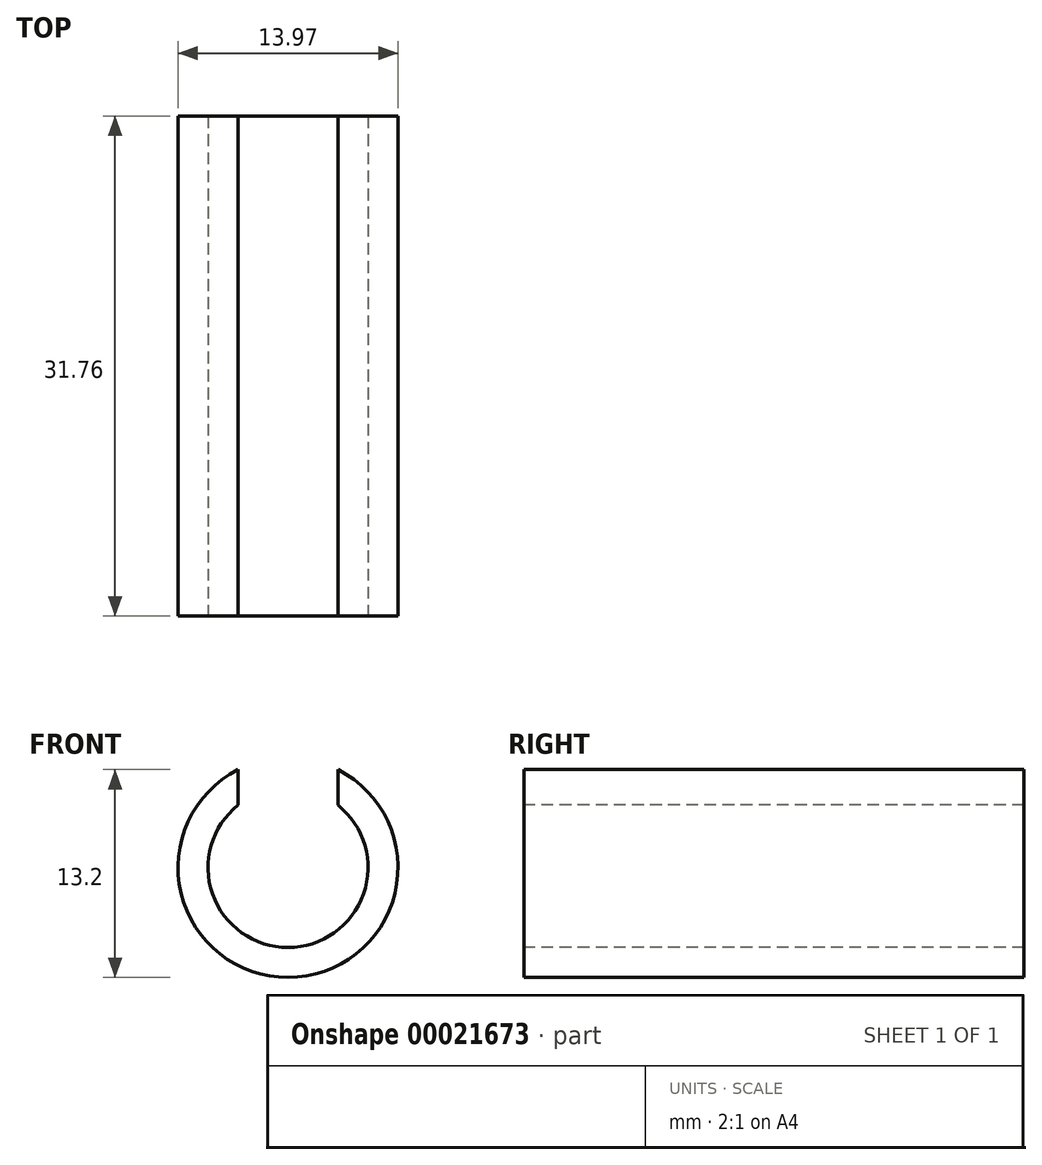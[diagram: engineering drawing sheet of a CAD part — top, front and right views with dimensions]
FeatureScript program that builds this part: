
annotation { "Feature Type Name" : "Feature", "Feature Type Description" : "" }
export const myFeature = defineFeature(function(context is Context, id is Id, definition is map)
    precondition{}
    {
        {
            var Q0;
            Q0=qCreatedBy(makeId("Front.planeOp"),FACE);
            var sketch = newSketch(context, id + "F0", { "sketchPlane" : qUnion([Q0])});
            skArc(sketch, "E0", {"start": v(-3.18, 3.97) * mm, "mid": v(0, -5.08) * mm, "end": v(3.18, 3.97) * mm});
            skPoint(sketch, "E1", {"position": v(-3.18, 3.97) * mm});
            skPoint(sketch, "E2", {"position": v(3.18, 3.97) * mm});
            skArc(sketch, "E3", {"start": v(-3.18, 6.22) * mm, "mid": v(0, -6.99) * mm, "end": v(3.17, 6.22) * mm});
            skPoint(sketch, "E4", {"position": v(-3.18, 6.22) * mm});
            skPoint(sketch, "E5", {"position": v(3.18, 6.22) * mm});
            skLineSegment(sketch, "E6", {"start": v(-3.18, 6.22) * mm, "end": v(-3.18, 3.97) * mm});
            skLineSegment(sketch, "E7", {"start": v(3.18, 6.22) * mm, "end": v(3.18, 3.97) * mm});
            skSolve(sketch);
        }
        {
            var Q0;
            Q0 = qSketchRegion(id + "F0", true);
            extrude(context, id + "F1", {"entities" : qUnion([Q0]), "endBound" : BoundingType.SYMMETRIC, "oppositeDirection" : true, "depth" : 31.75 * mm});
        }
    });
